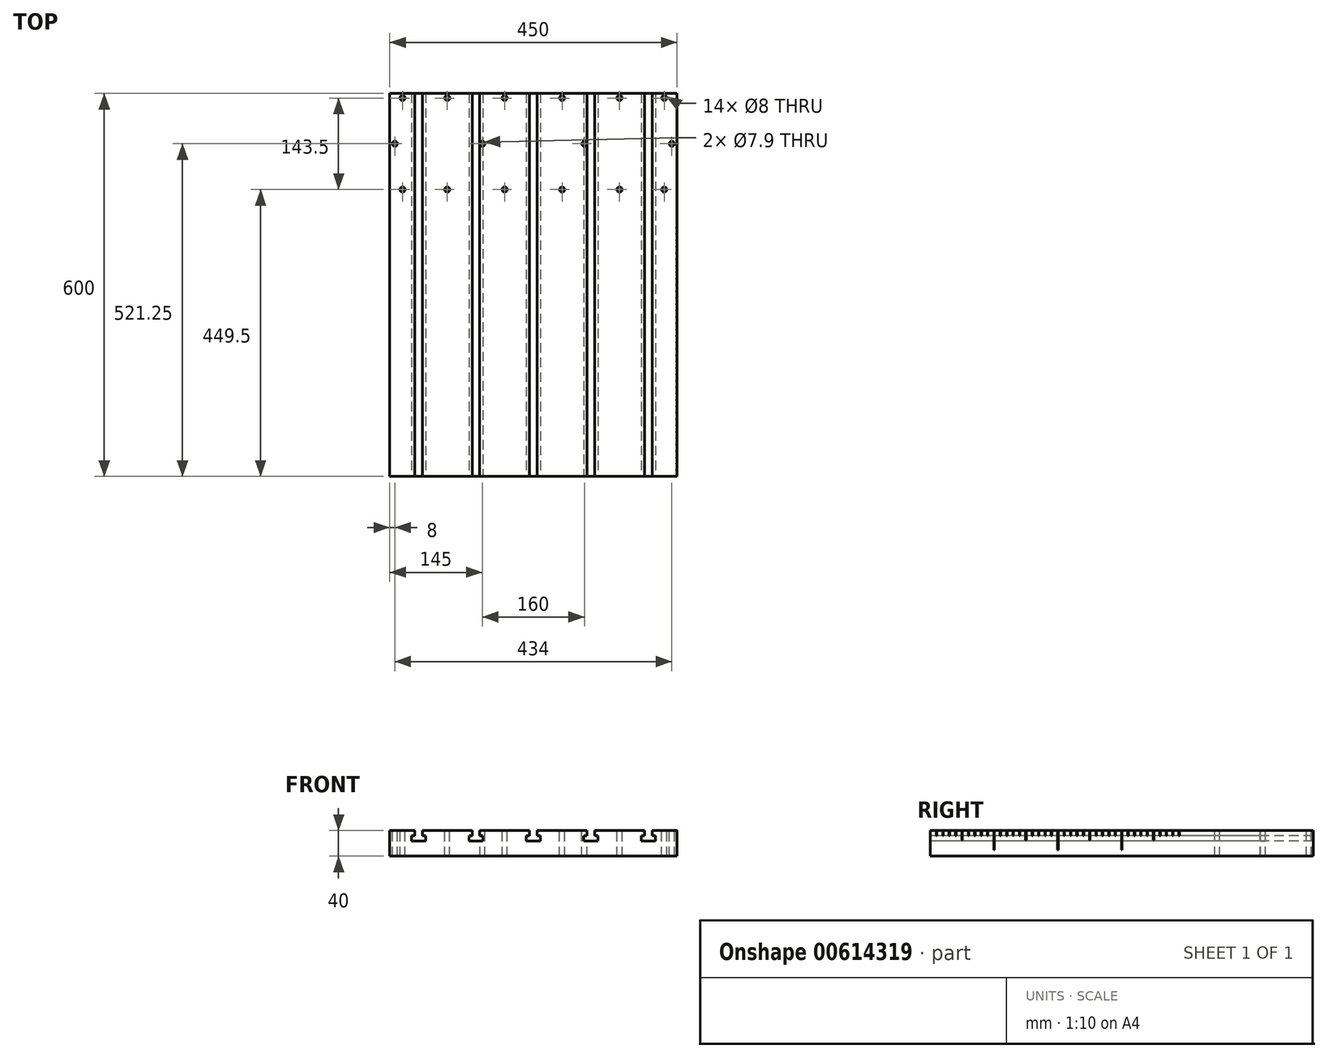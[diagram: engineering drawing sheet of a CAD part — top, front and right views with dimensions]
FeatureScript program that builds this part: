
annotation { "Feature Type Name" : "Feature", "Feature Type Description" : "" }
export const myFeature = defineFeature(function(context is Context, id is Id, definition is map)
    precondition{}
    {
        {
            var Q0;
            Q0=qCreatedBy(makeId("Front.planeOp"),FACE);
            var sketch = newSketch(context, id + "F0", { "sketchPlane" : qUnion([Q0])});
            skLineSegment(sketch, "E0.top", {"start": v(-225, 0) * mm, "end": v(225, 0) * mm});
            skLineSegment(sketch, "E0.left", {"start": v(-225, 40) * mm, "end": v(-225, 0) * mm});
            skLineSegment(sketch, "E0.right", {"start": v(225, 40) * mm, "end": v(225, 0) * mm});
            skLineSegment(sketch, "E1", {"start": v(-169, 24) * mm, "end": v(-169, 32) * mm});
            skLineSegment(sketch, "E2", {"start": v(-169, 32) * mm, "end": v(-174, 32) * mm});
            skLineSegment(sketch, "E3", {"start": v(-174, 32) * mm, "end": v(-174, 40) * mm});
            skLineSegment(sketch, "E4", {"start": v(-169, 24) * mm, "end": v(-191, 24) * mm});
            skLineSegment(sketch, "E5", {"start": v(-191, 24) * mm, "end": v(-191, 32) * mm});
            skLineSegment(sketch, "E6", {"start": v(-191, 32) * mm, "end": v(-186, 32) * mm});
            skLineSegment(sketch, "E7", {"start": v(-186, 32) * mm, "end": v(-186, 40) * mm});
            skLineSegment(sketch, "E8", {"start": v(-225, 40) * mm, "end": v(-186, 40) * mm});
            skLineSegment(sketch, "E9.1.0.0", {"start": v(-79, 24) * mm, "end": v(-101, 24) * mm});
            skLineSegment(sketch, "E9.1.0.1", {"start": v(-101, 24) * mm, "end": v(-101, 32) * mm});
            skLineSegment(sketch, "E9.1.0.2", {"start": v(-79, 24) * mm, "end": v(-79, 32) * mm});
            skLineSegment(sketch, "E9.1.0.3", {"start": v(-90, 40.27) * mm, "end": v(-90, 17.16) * mm, "construction": true});
            skLineSegment(sketch, "E9.1.0.4", {"start": v(-84, 32) * mm, "end": v(-84, 40) * mm});
            skLineSegment(sketch, "E9.1.0.5", {"start": v(-96, 32) * mm, "end": v(-96, 40) * mm});
            skLineSegment(sketch, "E9.1.0.6", {"start": v(-79, 32) * mm, "end": v(-84, 32) * mm});
            skLineSegment(sketch, "E9.1.0.7", {"start": v(-101, 32) * mm, "end": v(-96, 32) * mm});
            skLineSegment(sketch, "E9.2.0.0", {"start": v(11, 24) * mm, "end": v(-11, 24) * mm});
            skLineSegment(sketch, "E9.2.0.1", {"start": v(-11, 24) * mm, "end": v(-11, 32) * mm});
            skLineSegment(sketch, "E9.2.0.2", {"start": v(11, 24) * mm, "end": v(11, 32) * mm});
            skLineSegment(sketch, "E9.2.0.3", {"start": v(0, 40.27) * mm, "end": v(0, 17.16) * mm, "construction": true});
            skLineSegment(sketch, "E9.2.0.4", {"start": v(6, 32) * mm, "end": v(6, 40) * mm});
            skLineSegment(sketch, "E9.2.0.5", {"start": v(-6, 32) * mm, "end": v(-6, 40) * mm});
            skLineSegment(sketch, "E9.2.0.6", {"start": v(11, 32) * mm, "end": v(6, 32) * mm});
            skLineSegment(sketch, "E9.2.0.7", {"start": v(-11, 32) * mm, "end": v(-6, 32) * mm});
            skLineSegment(sketch, "E9.3.0.0", {"start": v(101, 24) * mm, "end": v(79, 24) * mm});
            skLineSegment(sketch, "E9.3.0.1", {"start": v(79, 24) * mm, "end": v(79, 32) * mm});
            skLineSegment(sketch, "E9.3.0.2", {"start": v(101, 24) * mm, "end": v(101, 32) * mm});
            skLineSegment(sketch, "E9.3.0.3", {"start": v(90, 40.27) * mm, "end": v(90, 17.16) * mm, "construction": true});
            skLineSegment(sketch, "E9.3.0.4", {"start": v(96, 32) * mm, "end": v(96, 40) * mm});
            skLineSegment(sketch, "E9.3.0.5", {"start": v(84, 32) * mm, "end": v(84, 40) * mm});
            skLineSegment(sketch, "E9.3.0.6", {"start": v(101, 32) * mm, "end": v(96, 32) * mm});
            skLineSegment(sketch, "E9.3.0.7", {"start": v(79, 32) * mm, "end": v(84, 32) * mm});
            skLineSegment(sketch, "E9.4.0.0", {"start": v(191, 24) * mm, "end": v(169, 24) * mm});
            skLineSegment(sketch, "E9.4.0.1", {"start": v(169, 24) * mm, "end": v(169, 32) * mm});
            skLineSegment(sketch, "E9.4.0.2", {"start": v(191, 24) * mm, "end": v(191, 32) * mm});
            skLineSegment(sketch, "E9.4.0.3", {"start": v(180, 40.27) * mm, "end": v(180, 17.16) * mm, "construction": true});
            skLineSegment(sketch, "E9.4.0.4", {"start": v(186, 32) * mm, "end": v(186, 40) * mm});
            skLineSegment(sketch, "E9.4.0.5", {"start": v(174, 32) * mm, "end": v(174, 40) * mm});
            skLineSegment(sketch, "E9.4.0.6", {"start": v(191, 32) * mm, "end": v(186, 32) * mm});
            skLineSegment(sketch, "E9.4.0.7", {"start": v(169, 32) * mm, "end": v(174, 32) * mm});
            skLineSegment(sketch, "E9.direction1", {"start": v(-191, 24) * mm, "end": v(-101, 24) * mm, "construction": true});
            skLineSegment(sketch, "E10", {"start": v(-174, 40) * mm, "end": v(-96, 40) * mm});
            skLineSegment(sketch, "E11", {"start": v(-84, 40) * mm, "end": v(-6, 40) * mm});
            skLineSegment(sketch, "E12", {"start": v(6, 40) * mm, "end": v(84, 40) * mm});
            skLineSegment(sketch, "E13", {"start": v(96, 40) * mm, "end": v(174, 40) * mm});
            skLineSegment(sketch, "E14", {"start": v(186, 40) * mm, "end": v(225, 40) * mm});
            skLineSegment(sketch, "E15", {"start": v(225, 40) * mm, "end": v(225, 40) * mm});
            skSolve(sketch);
        }
        {
            var Q0;
            Q0=makeQuery(id+"F0.imprint","IMPRINT",FACE,{"disambiguationData":[TD([[makeQuery(id+"F0.imprint","IMPRINT",EDGE,{"derivedFrom":sQuery(id+"F0.wireOp",EDGE,"E0.top")}),1.0]])]});
            extrude(context, id + "F1", {"entities" : qUnion([Q0]), "oppositeDirection" : true, "depth" : 600 * mm, "offsetDistance" : 25 * mm});
        }
        {
            var Q0;
            Q0=makeQuery(id+"F1.opExtrude","SWEPT_FACE",FACE,{"disambiguationData":[OSD([sQuery(id+"F0.wireOp",EDGE,"E10")])]});
            var sketch = newSketch(context, id + "F2", { "sketchPlane" : qUnion([Q0])});
            skLineSegment(sketch, "E16", {"start": v(-225, 326.2) * mm, "end": v(225, 326.2) * mm});
            skPoint(sketch, "E17", {"position": v(0, 326.2) * mm});
            skCircle(sketch, "E18", {"center": v(225, 0) * mm, "radius": 0.25 * mm});
            skCircle(sketch, "E19.0.1.0", {"center": v(225, 10) * mm, "radius": 0.5 * mm});
            skCircle(sketch, "E19.0.2.0", {"center": v(225, 20) * mm, "radius": 0.5 * mm});
            skCircle(sketch, "E19.0.3.0", {"center": v(225, 30) * mm, "radius": 0.5 * mm});
            skCircle(sketch, "E19.0.4.0", {"center": v(225, 40) * mm, "radius": 0.5 * mm});
            skCircle(sketch, "E19.0.5.0", {"center": v(225, 50) * mm, "radius": 0.5 * mm});
            skCircle(sketch, "E19.0.6.0", {"center": v(225, 60) * mm, "radius": 0.5 * mm});
            skCircle(sketch, "E19.0.7.0", {"center": v(225, 70) * mm, "radius": 0.5 * mm});
            skCircle(sketch, "E19.0.8.0", {"center": v(225, 80) * mm, "radius": 0.5 * mm});
            skCircle(sketch, "E19.0.9.0", {"center": v(225, 90) * mm, "radius": 0.5 * mm});
            skCircle(sketch, "E19.0.10.0", {"center": v(225, 100) * mm, "radius": 0.5 * mm});
            skCircle(sketch, "E19.0.11.0", {"center": v(225, 110) * mm, "radius": 0.5 * mm});
            skCircle(sketch, "E19.0.12.0", {"center": v(225, 120) * mm, "radius": 0.5 * mm});
            skCircle(sketch, "E19.0.13.0", {"center": v(225, 130) * mm, "radius": 0.5 * mm});
            skCircle(sketch, "E19.0.14.0", {"center": v(225, 140) * mm, "radius": 0.5 * mm});
            skCircle(sketch, "E19.0.15.0", {"center": v(225, 150) * mm, "radius": 0.5 * mm});
            skCircle(sketch, "E19.0.16.0", {"center": v(225, 160) * mm, "radius": 0.5 * mm});
            skCircle(sketch, "E19.0.17.0", {"center": v(225, 170) * mm, "radius": 0.5 * mm});
            skCircle(sketch, "E19.0.18.0", {"center": v(225, 180) * mm, "radius": 0.5 * mm});
            skCircle(sketch, "E19.0.19.0", {"center": v(225, 190) * mm, "radius": 0.5 * mm});
            skCircle(sketch, "E19.0.20.0", {"center": v(225, 200) * mm, "radius": 0.5 * mm});
            skCircle(sketch, "E19.0.21.0", {"center": v(225, 210) * mm, "radius": 0.5 * mm});
            skCircle(sketch, "E19.0.22.0", {"center": v(225, 220) * mm, "radius": 0.5 * mm});
            skCircle(sketch, "E19.0.23.0", {"center": v(225, 230) * mm, "radius": 0.5 * mm});
            skCircle(sketch, "E19.0.24.0", {"center": v(225, 240) * mm, "radius": 0.5 * mm});
            skCircle(sketch, "E19.0.25.0", {"center": v(225, 250) * mm, "radius": 0.5 * mm});
            skCircle(sketch, "E19.0.26.0", {"center": v(225, 260) * mm, "radius": 0.5 * mm});
            skCircle(sketch, "E19.0.27.0", {"center": v(225, 270) * mm, "radius": 0.5 * mm});
            skCircle(sketch, "E19.0.28.0", {"center": v(225, 280) * mm, "radius": 0.5 * mm});
            skCircle(sketch, "E19.0.29.0", {"center": v(225, 290) * mm, "radius": 0.5 * mm});
            skCircle(sketch, "E19.0.30.0", {"center": v(225, 300) * mm, "radius": 0.5 * mm});
            skCircle(sketch, "E19.0.31.0", {"center": v(225, 310) * mm, "radius": 0.5 * mm});
            skCircle(sketch, "E19.0.32.0", {"center": v(225, 320) * mm, "radius": 0.5 * mm});
            skCircle(sketch, "E19.0.33.0", {"center": v(225, 330) * mm, "radius": 0.5 * mm});
            skCircle(sketch, "E19.0.34.0", {"center": v(225, 340) * mm, "radius": 0.5 * mm});
            skCircle(sketch, "E19.0.35.0", {"center": v(225, 350) * mm, "radius": 0.5 * mm});
            skCircle(sketch, "E19.0.36.0", {"center": v(225, 360) * mm, "radius": 0.5 * mm});
            skCircle(sketch, "E19.0.37.0", {"center": v(225, 370) * mm, "radius": 0.5 * mm});
            skCircle(sketch, "E19.0.38.0", {"center": v(225, 380) * mm, "radius": 0.5 * mm});
            skCircle(sketch, "E19.0.39.0", {"center": v(225, 390) * mm, "radius": 0.5 * mm});
            skLineSegment(sketch, "E19.direction2", {"start": v(225, 0) * mm, "end": v(225, 10) * mm, "construction": true});
            skLineSegment(sketch, "E20", {"start": v(225.64, 593) * mm, "end": v(-225.44, 593) * mm, "construction": true});
            skLineSegment(sketch, "E21", {"start": v(-225.44, 449.5) * mm, "end": v(225.64, 449.5) * mm, "construction": true});
            skLineSegment(sketch, "E22", {"start": v(80, 449.5) * mm, "end": v(80, 593) * mm, "construction": true});
            skPoint(sketch, "E23", {"position": v(0, 593) * mm});
            skLineSegment(sketch, "E24", {"start": v(-80, 593) * mm, "end": v(-80, 449.5) * mm, "construction": true});
            skCircle(sketch, "E25", {"center": v(80, 521.25) * mm, "radius": 3.95 * mm});
            skCircle(sketch, "E26", {"center": v(-80, 521.25) * mm, "radius": 3.95 * mm});
            skCircle(sketch, "E27", {"center": v(-45, 593) * mm, "radius": 4 * mm});
            skCircle(sketch, "E28", {"center": v(-135, 593) * mm, "radius": 4 * mm});
            skCircle(sketch, "E29", {"center": v(-205, 593) * mm, "radius": 4 * mm});
            skCircle(sketch, "E30", {"center": v(-45, 449.5) * mm, "radius": 4 * mm});
            skCircle(sketch, "E31", {"center": v(-135, 449.5) * mm, "radius": 4 * mm});
            skCircle(sketch, "E32", {"center": v(-205, 449.5) * mm, "radius": 4 * mm});
            skCircle(sketch, "E33", {"center": v(-217, 521.25) * mm, "radius": 4 * mm});
            skCircle(sketch, "E34", {"center": v(45, 449.5) * mm, "radius": 4 * mm});
            skCircle(sketch, "E35", {"center": v(45, 593) * mm, "radius": 4 * mm});
            skCircle(sketch, "E36", {"center": v(135, 593) * mm, "radius": 4 * mm});
            skCircle(sketch, "E37", {"center": v(205, 593) * mm, "radius": 4 * mm});
            skCircle(sketch, "E38", {"center": v(217, 521.25) * mm, "radius": 4 * mm});
            skCircle(sketch, "E39", {"center": v(135, 449.5) * mm, "radius": 4 * mm});
            skCircle(sketch, "E40", {"center": v(205, 449.5) * mm, "radius": 4 * mm});
            skLineSegment(sketch, "E41", {"start": v(224.94, 442.5) * mm, "end": v(-225.54, 442.5) * mm});
            skSolve(sketch);
        }
        {
            var Q0;
            Q0=makeQuery(id+"F2.imprint","IMPRINT",FACE,{"disambiguationData":[TD([[makeQuery(id+"F2.imprint","IMPRINT",EDGE,{"derivedFrom":sQuery(id+"F2.wireOp",EDGE,"E18")}),1.0]])]});
            var Q1;
            Q1=makeQuery(id+"F2.imprint","IMPRINT",FACE,{"disambiguationData":[TD([[makeQuery(id+"F2.imprint","IMPRINT",EDGE,{"derivedFrom":sQuery(id+"F2.wireOp",EDGE,"E19.0.1.0")}),1.0]])]});
            var Q2;
            Q2=makeQuery(id+"F2.imprint","IMPRINT",FACE,{"disambiguationData":[TD([[makeQuery(id+"F2.imprint","IMPRINT",EDGE,{"derivedFrom":sQuery(id+"F2.wireOp",EDGE,"E19.0.2.0")}),1.0]])]});
            var Q3;
            Q3=makeQuery(id+"F2.imprint","IMPRINT",FACE,{"disambiguationData":[TD([[makeQuery(id+"F2.imprint","IMPRINT",EDGE,{"derivedFrom":sQuery(id+"F2.wireOp",EDGE,"E19.0.3.0")}),1.0]])]});
            var Q4;
            Q4=makeQuery(id+"F2.imprint","IMPRINT",FACE,{"disambiguationData":[TD([[makeQuery(id+"F2.imprint","IMPRINT",EDGE,{"derivedFrom":sQuery(id+"F2.wireOp",EDGE,"E19.0.4.0")}),1.0]])]});
            var Q5;
            Q5=makeQuery(id+"F2.imprint","IMPRINT",FACE,{"disambiguationData":[TD([[makeQuery(id+"F2.imprint","IMPRINT",EDGE,{"derivedFrom":sQuery(id+"F2.wireOp",EDGE,"E19.0.5.0")}),1.0]])]});
            var Q6;
            Q6=makeQuery(id+"F2.imprint","IMPRINT",FACE,{"disambiguationData":[TD([[makeQuery(id+"F2.imprint","IMPRINT",EDGE,{"derivedFrom":sQuery(id+"F2.wireOp",EDGE,"E19.0.6.0")}),1.0]])]});
            var Q7;
            Q7=makeQuery(id+"F2.imprint","IMPRINT",FACE,{"disambiguationData":[TD([[makeQuery(id+"F2.imprint","IMPRINT",EDGE,{"derivedFrom":sQuery(id+"F2.wireOp",EDGE,"E19.0.7.0")}),1.0]])]});
            var Q8;
            Q8=makeQuery(id+"F2.imprint","IMPRINT",FACE,{"disambiguationData":[TD([[makeQuery(id+"F2.imprint","IMPRINT",EDGE,{"derivedFrom":sQuery(id+"F2.wireOp",EDGE,"E19.0.8.0")}),1.0]])]});
            var Q9;
            Q9=makeQuery(id+"F2.imprint","IMPRINT",FACE,{"disambiguationData":[TD([[makeQuery(id+"F2.imprint","IMPRINT",EDGE,{"derivedFrom":sQuery(id+"F2.wireOp",EDGE,"E19.0.9.0")}),1.0]])]});
            var Q10;
            Q10=makeQuery(id+"F2.imprint","IMPRINT",FACE,{"disambiguationData":[TD([[makeQuery(id+"F2.imprint","IMPRINT",EDGE,{"derivedFrom":sQuery(id+"F2.wireOp",EDGE,"E19.0.10.0")}),1.0]])]});
            var Q11;
            Q11=makeQuery(id+"F2.imprint","IMPRINT",FACE,{"disambiguationData":[TD([[makeQuery(id+"F2.imprint","IMPRINT",EDGE,{"derivedFrom":sQuery(id+"F2.wireOp",EDGE,"E19.0.11.0")}),1.0]])]});
            var Q12;
            Q12=makeQuery(id+"F2.imprint","IMPRINT",FACE,{"disambiguationData":[TD([[makeQuery(id+"F2.imprint","IMPRINT",EDGE,{"derivedFrom":sQuery(id+"F2.wireOp",EDGE,"E19.0.12.0")}),1.0]])]});
            var Q13;
            Q13=makeQuery(id+"F2.imprint","IMPRINT",FACE,{"disambiguationData":[TD([[makeQuery(id+"F2.imprint","IMPRINT",EDGE,{"derivedFrom":sQuery(id+"F2.wireOp",EDGE,"E19.0.13.0")}),1.0]])]});
            var Q14;
            Q14=makeQuery(id+"F2.imprint","IMPRINT",FACE,{"disambiguationData":[TD([[makeQuery(id+"F2.imprint","IMPRINT",EDGE,{"derivedFrom":sQuery(id+"F2.wireOp",EDGE,"E19.0.14.0")}),1.0]])]});
            var Q15;
            Q15=makeQuery(id+"F2.imprint","IMPRINT",FACE,{"disambiguationData":[TD([[makeQuery(id+"F2.imprint","IMPRINT",EDGE,{"derivedFrom":sQuery(id+"F2.wireOp",EDGE,"E19.0.15.0")}),1.0]])]});
            var Q16;
            Q16=makeQuery(id+"F2.imprint","IMPRINT",FACE,{"disambiguationData":[TD([[makeQuery(id+"F2.imprint","IMPRINT",EDGE,{"derivedFrom":sQuery(id+"F2.wireOp",EDGE,"E19.0.16.0")}),1.0]])]});
            var Q17;
            Q17=makeQuery(id+"F2.imprint","IMPRINT",FACE,{"disambiguationData":[TD([[makeQuery(id+"F2.imprint","IMPRINT",EDGE,{"derivedFrom":sQuery(id+"F2.wireOp",EDGE,"E19.0.17.0")}),1.0]])]});
            var Q18;
            Q18=makeQuery(id+"F2.imprint","IMPRINT",FACE,{"disambiguationData":[TD([[makeQuery(id+"F2.imprint","IMPRINT",EDGE,{"derivedFrom":sQuery(id+"F2.wireOp",EDGE,"E19.0.18.0")}),1.0]])]});
            var Q19;
            Q19=makeQuery(id+"F2.imprint","IMPRINT",FACE,{"disambiguationData":[TD([[makeQuery(id+"F2.imprint","IMPRINT",EDGE,{"derivedFrom":sQuery(id+"F2.wireOp",EDGE,"E19.0.19.0")}),1.0]])]});
            var Q20;
            Q20=makeQuery(id+"F2.imprint","IMPRINT",FACE,{"disambiguationData":[TD([[makeQuery(id+"F2.imprint","IMPRINT",EDGE,{"derivedFrom":sQuery(id+"F2.wireOp",EDGE,"E19.0.20.0")}),1.0]])]});
            var Q21;
            Q21=makeQuery(id+"F2.imprint","IMPRINT",FACE,{"disambiguationData":[TD([[makeQuery(id+"F2.imprint","IMPRINT",EDGE,{"derivedFrom":sQuery(id+"F2.wireOp",EDGE,"E19.0.21.0")}),1.0]])]});
            var Q22;
            Q22=makeQuery(id+"F2.imprint","IMPRINT",FACE,{"disambiguationData":[TD([[makeQuery(id+"F2.imprint","IMPRINT",EDGE,{"derivedFrom":sQuery(id+"F2.wireOp",EDGE,"E19.0.22.0")}),1.0]])]});
            var Q23;
            Q23=makeQuery(id+"F2.imprint","IMPRINT",FACE,{"disambiguationData":[TD([[makeQuery(id+"F2.imprint","IMPRINT",EDGE,{"derivedFrom":sQuery(id+"F2.wireOp",EDGE,"E19.0.23.0")}),1.0]])]});
            var Q24;
            Q24=makeQuery(id+"F2.imprint","IMPRINT",FACE,{"disambiguationData":[TD([[makeQuery(id+"F2.imprint","IMPRINT",EDGE,{"derivedFrom":sQuery(id+"F2.wireOp",EDGE,"E19.0.24.0")}),1.0]])]});
            var Q25;
            Q25=makeQuery(id+"F2.imprint","IMPRINT",FACE,{"disambiguationData":[TD([[makeQuery(id+"F2.imprint","IMPRINT",EDGE,{"derivedFrom":sQuery(id+"F2.wireOp",EDGE,"E19.0.25.0")}),1.0]])]});
            var Q26;
            Q26=makeQuery(id+"F2.imprint","IMPRINT",FACE,{"disambiguationData":[TD([[makeQuery(id+"F2.imprint","IMPRINT",EDGE,{"derivedFrom":sQuery(id+"F2.wireOp",EDGE,"E19.0.26.0")}),1.0]])]});
            var Q27;
            Q27=makeQuery(id+"F2.imprint","IMPRINT",FACE,{"disambiguationData":[TD([[makeQuery(id+"F2.imprint","IMPRINT",EDGE,{"derivedFrom":sQuery(id+"F2.wireOp",EDGE,"E19.0.27.0")}),1.0]])]});
            var Q28;
            Q28=makeQuery(id+"F2.imprint","IMPRINT",FACE,{"disambiguationData":[TD([[makeQuery(id+"F2.imprint","IMPRINT",EDGE,{"derivedFrom":sQuery(id+"F2.wireOp",EDGE,"E19.0.28.0")}),1.0]])]});
            var Q29;
            Q29=makeQuery(id+"F2.imprint","IMPRINT",FACE,{"disambiguationData":[TD([[makeQuery(id+"F2.imprint","IMPRINT",EDGE,{"derivedFrom":sQuery(id+"F2.wireOp",EDGE,"E19.0.29.0")}),1.0]])]});
            var Q30;
            Q30=makeQuery(id+"F2.imprint","IMPRINT",FACE,{"disambiguationData":[TD([[makeQuery(id+"F2.imprint","IMPRINT",EDGE,{"derivedFrom":sQuery(id+"F2.wireOp",EDGE,"E19.0.30.0")}),1.0]])]});
            var Q31;
            Q31=makeQuery(id+"F2.imprint","IMPRINT",FACE,{"disambiguationData":[TD([[makeQuery(id+"F2.imprint","IMPRINT",EDGE,{"derivedFrom":sQuery(id+"F2.wireOp",EDGE,"E19.0.31.0")}),1.0]])]});
            var Q32;
            Q32=makeQuery(id+"F2.imprint","IMPRINT",FACE,{"disambiguationData":[TD([[makeQuery(id+"F2.imprint","IMPRINT",EDGE,{"derivedFrom":sQuery(id+"F2.wireOp",EDGE,"E19.0.32.0")}),1.0]])]});
            var Q33;
            Q33=makeQuery(id+"F2.imprint","IMPRINT",FACE,{"disambiguationData":[TD([[makeQuery(id+"F2.imprint","IMPRINT",EDGE,{"derivedFrom":sQuery(id+"F2.wireOp",EDGE,"E19.0.33.0")}),1.0]])]});
            var Q34;
            Q34=makeQuery(id+"F2.imprint","IMPRINT",FACE,{"disambiguationData":[TD([[makeQuery(id+"F2.imprint","IMPRINT",EDGE,{"derivedFrom":sQuery(id+"F2.wireOp",EDGE,"E19.0.34.0")}),1.0]])]});
            var Q35;
            Q35=makeQuery(id+"F2.imprint","IMPRINT",FACE,{"disambiguationData":[TD([[makeQuery(id+"F2.imprint","IMPRINT",EDGE,{"derivedFrom":sQuery(id+"F2.wireOp",EDGE,"E19.0.35.0")}),1.0]])]});
            var Q36;
            Q36=makeQuery(id+"F2.imprint","IMPRINT",FACE,{"disambiguationData":[TD([[makeQuery(id+"F2.imprint","IMPRINT",EDGE,{"derivedFrom":sQuery(id+"F2.wireOp",EDGE,"E19.0.36.0")}),1.0]])]});
            var Q37;
            Q37=makeQuery(id+"F2.imprint","IMPRINT",FACE,{"disambiguationData":[TD([[makeQuery(id+"F2.imprint","IMPRINT",EDGE,{"derivedFrom":sQuery(id+"F2.wireOp",EDGE,"E19.0.37.0")}),1.0]])]});
            var Q38;
            Q38=makeQuery(id+"F2.imprint","IMPRINT",FACE,{"disambiguationData":[TD([[makeQuery(id+"F2.imprint","IMPRINT",EDGE,{"derivedFrom":sQuery(id+"F2.wireOp",EDGE,"E19.0.38.0")}),1.0]])]});
            var Q39;
            Q39=makeQuery(id+"F2.imprint","IMPRINT",FACE,{"disambiguationData":[TD([[makeQuery(id+"F2.imprint","IMPRINT",EDGE,{"derivedFrom":sQuery(id+"F2.wireOp",EDGE,"E19.0.39.0")}),1.0]])]});
            extrude(context, id + "F3", {"entities" : qUnion([Q0, Q1, Q2, Q3, Q4, Q5, Q6, Q7, Q8, Q9, Q10, Q11, Q12, Q13, Q14, Q15, Q16, Q17, Q18, Q19, Q20, Q21, Q22, Q23, Q24, Q25, Q26, Q27, Q28, Q29, Q30, Q31, Q32, Q33, Q34, Q35, Q36, Q37, Q38, Q39]), "operationType" : NewBodyOperationType.REMOVE, "oppositeDirection" : true, "depth" : 8 * mm, "offsetDistance" : 25 * mm});
        }
        {
            var Q0;
            Q0=makeQuery(id+"F2.imprint","IMPRINT",FACE,{"disambiguationData":[TD([[makeQuery(id+"F2.imprint","IMPRINT",EDGE,{"derivedFrom":sQuery(id+"F2.wireOp",EDGE,"E19.0.5.0")}),1.0]])]});
            var Q1;
            Q1=makeQuery(id+"F2.imprint","IMPRINT",FACE,{"disambiguationData":[TD([[makeQuery(id+"F2.imprint","IMPRINT",EDGE,{"derivedFrom":sQuery(id+"F2.wireOp",EDGE,"E19.0.10.0")}),1.0]])]});
            var Q2;
            Q2=makeQuery(id+"F2.imprint","IMPRINT",FACE,{"disambiguationData":[TD([[makeQuery(id+"F2.imprint","IMPRINT",EDGE,{"derivedFrom":sQuery(id+"F2.wireOp",EDGE,"E19.0.15.0")}),1.0]])]});
            var Q3;
            Q3=makeQuery(id+"F2.imprint","IMPRINT",FACE,{"disambiguationData":[TD([[makeQuery(id+"F2.imprint","IMPRINT",EDGE,{"derivedFrom":sQuery(id+"F2.wireOp",EDGE,"E19.0.20.0")}),1.0]])]});
            var Q4;
            Q4=makeQuery(id+"F2.imprint","IMPRINT",FACE,{"disambiguationData":[TD([[makeQuery(id+"F2.imprint","IMPRINT",EDGE,{"derivedFrom":sQuery(id+"F2.wireOp",EDGE,"E19.0.25.0")}),1.0]])]});
            var Q5;
            Q5=makeQuery(id+"F2.imprint","IMPRINT",FACE,{"disambiguationData":[TD([[makeQuery(id+"F2.imprint","IMPRINT",EDGE,{"derivedFrom":sQuery(id+"F2.wireOp",EDGE,"E19.0.30.0")}),1.0]])]});
            var Q6;
            Q6=makeQuery(id+"F2.imprint","IMPRINT",FACE,{"disambiguationData":[TD([[makeQuery(id+"F2.imprint","IMPRINT",EDGE,{"derivedFrom":sQuery(id+"F2.wireOp",EDGE,"E19.0.35.0")}),1.0]])]});
            extrude(context, id + "F4", {"entities" : qUnion([Q0, Q1, Q2, Q3, Q4, Q5, Q6]), "operationType" : NewBodyOperationType.REMOVE, "oppositeDirection" : true, "depth" : 15 * mm, "offsetDistance" : 25 * mm});
        }
        {
            var Q0;
            Q0=makeQuery(id+"F2.imprint","IMPRINT",FACE,{"disambiguationData":[TD([[makeQuery(id+"F2.imprint","IMPRINT",EDGE,{"derivedFrom":sQuery(id+"F2.wireOp",EDGE,"E18")}),1.0]])]});
            var Q1;
            Q1=makeQuery(id+"F2.imprint","IMPRINT",FACE,{"disambiguationData":[TD([[makeQuery(id+"F2.imprint","IMPRINT",EDGE,{"derivedFrom":sQuery(id+"F2.wireOp",EDGE,"E19.0.10.0")}),1.0]])]});
            var Q2;
            Q2=makeQuery(id+"F2.imprint","IMPRINT",FACE,{"disambiguationData":[TD([[makeQuery(id+"F2.imprint","IMPRINT",EDGE,{"derivedFrom":sQuery(id+"F2.wireOp",EDGE,"E19.0.20.0")}),1.0]])]});
            var Q3;
            Q3=makeQuery(id+"F2.imprint","IMPRINT",FACE,{"disambiguationData":[TD([[makeQuery(id+"F2.imprint","IMPRINT",EDGE,{"derivedFrom":sQuery(id+"F2.wireOp",EDGE,"E19.0.30.0")}),1.0]])]});
            extrude(context, id + "F5", {"entities" : qUnion([Q0, Q1, Q2, Q3]), "operationType" : NewBodyOperationType.REMOVE, "oppositeDirection" : true, "depth" : 30 * mm, "offsetDistance" : 25 * mm});
        }
        {
            var Q0;
            Q0=makeQuery(id+"F2.imprint","IMPRINT",FACE,{"disambiguationData":[TD([[makeQuery(id+"F2.imprint","IMPRINT",EDGE,{"derivedFrom":sQuery(id+"F2.wireOp",EDGE,"E27")}),1.0]])]});
            var Q1;
            Q1=makeQuery(id+"F2.imprint","IMPRINT",FACE,{"disambiguationData":[TD([[makeQuery(id+"F2.imprint","IMPRINT",EDGE,{"derivedFrom":sQuery(id+"F2.wireOp",EDGE,"E28")}),1.0]])]});
            var Q2;
            Q2=makeQuery(id+"F2.imprint","IMPRINT",FACE,{"disambiguationData":[TD([[makeQuery(id+"F2.imprint","IMPRINT",EDGE,{"derivedFrom":sQuery(id+"F2.wireOp",EDGE,"E29")}),1.0]])]});
            var Q3;
            Q3=makeQuery(id+"F2.imprint","IMPRINT",FACE,{"disambiguationData":[TD([[makeQuery(id+"F2.imprint","IMPRINT",EDGE,{"derivedFrom":sQuery(id+"F2.wireOp",EDGE,"E33")}),1.0]])]});
            var Q4;
            Q4=makeQuery(id+"F2.imprint","IMPRINT",FACE,{"disambiguationData":[TD([[makeQuery(id+"F2.imprint","IMPRINT",EDGE,{"derivedFrom":sQuery(id+"F2.wireOp",EDGE,"E32")}),1.0]])]});
            var Q5;
            Q5=makeQuery(id+"F2.imprint","IMPRINT",FACE,{"disambiguationData":[TD([[makeQuery(id+"F2.imprint","IMPRINT",EDGE,{"derivedFrom":sQuery(id+"F2.wireOp",EDGE,"E30")}),1.0]])]});
            var Q6;
            Q6=makeQuery(id+"F2.imprint","IMPRINT",FACE,{"disambiguationData":[TD([[makeQuery(id+"F2.imprint","IMPRINT",EDGE,{"derivedFrom":sQuery(id+"F2.wireOp",EDGE,"E31")}),1.0]])]});
            var Q7;
            Q7=makeQuery(id+"F2.imprint","IMPRINT",FACE,{"disambiguationData":[TD([[makeQuery(id+"F2.imprint","IMPRINT",EDGE,{"derivedFrom":sQuery(id+"F2.wireOp",EDGE,"E35")}),1.0]])]});
            var Q8;
            Q8=makeQuery(id+"F2.imprint","IMPRINT",FACE,{"disambiguationData":[TD([[makeQuery(id+"F2.imprint","IMPRINT",EDGE,{"derivedFrom":sQuery(id+"F2.wireOp",EDGE,"E36")}),1.0]])]});
            var Q9;
            Q9=makeQuery(id+"F2.imprint","IMPRINT",FACE,{"disambiguationData":[TD([[makeQuery(id+"F2.imprint","IMPRINT",EDGE,{"derivedFrom":sQuery(id+"F2.wireOp",EDGE,"E37")}),1.0]])]});
            var Q10;
            Q10=makeQuery(id+"F2.imprint","IMPRINT",FACE,{"disambiguationData":[TD([[makeQuery(id+"F2.imprint","IMPRINT",EDGE,{"derivedFrom":sQuery(id+"F2.wireOp",EDGE,"E38")}),1.0]])]});
            var Q11;
            Q11=makeQuery(id+"F2.imprint","IMPRINT",FACE,{"disambiguationData":[TD([[makeQuery(id+"F2.imprint","IMPRINT",EDGE,{"derivedFrom":sQuery(id+"F2.wireOp",EDGE,"E34")}),1.0]])]});
            var Q12;
            Q12=makeQuery(id+"F2.imprint","IMPRINT",FACE,{"disambiguationData":[TD([[makeQuery(id+"F2.imprint","IMPRINT",EDGE,{"derivedFrom":sQuery(id+"F2.wireOp",EDGE,"E40")}),1.0]])]});
            var Q13;
            Q13=makeQuery(id+"F2.imprint","IMPRINT",FACE,{"disambiguationData":[TD([[makeQuery(id+"F2.imprint","IMPRINT",EDGE,{"derivedFrom":sQuery(id+"F2.wireOp",EDGE,"E39")}),1.0]])]});
            var Q14;
            Q14=makeQuery(id+"F2.imprint","IMPRINT",FACE,{"disambiguationData":[TD([[makeQuery(id+"F2.imprint","IMPRINT",EDGE,{"derivedFrom":sQuery(id+"F2.wireOp",EDGE,"E25")}),1.0]])]});
            var Q15;
            Q15=makeQuery(id+"F2.imprint","IMPRINT",FACE,{"disambiguationData":[TD([[makeQuery(id+"F2.imprint","IMPRINT",EDGE,{"derivedFrom":sQuery(id+"F2.wireOp",EDGE,"E26")}),1.0]])]});
            extrude(context, id + "F6", {"entities" : qUnion([Q0, Q1, Q2, Q3, Q4, Q5, Q6, Q7, Q8, Q9, Q10, Q11, Q12, Q13, Q14, Q15]), "operationType" : NewBodyOperationType.REMOVE, "endBound" : BoundingType.THROUGH_ALL, "oppositeDirection" : true, "depth" : 20 * mm, "offsetDistance" : 25 * mm});
        }
    });
